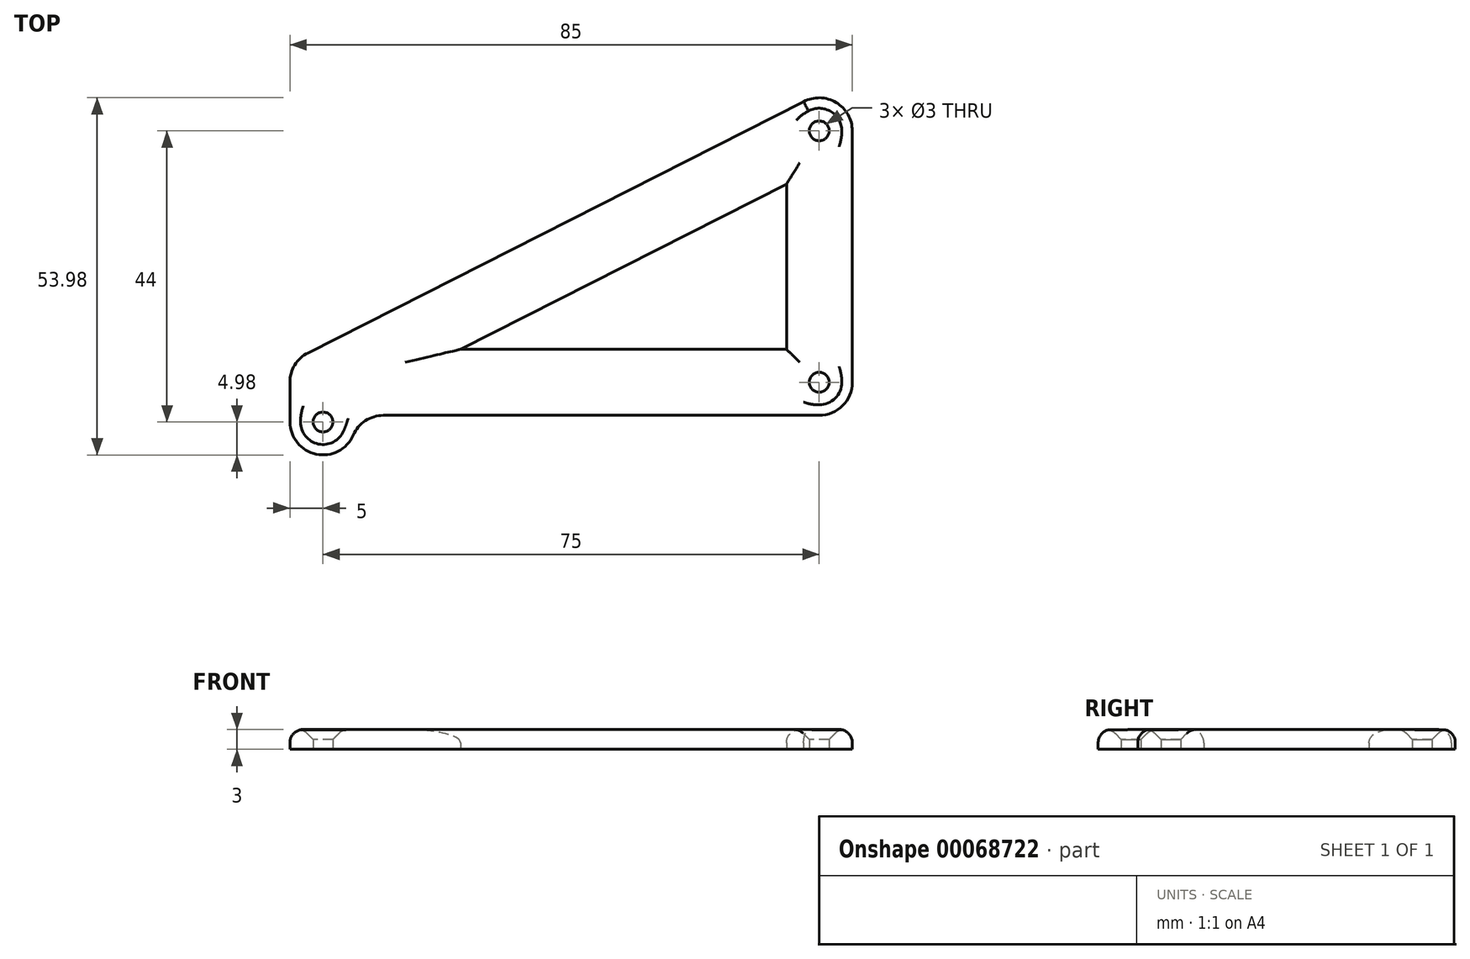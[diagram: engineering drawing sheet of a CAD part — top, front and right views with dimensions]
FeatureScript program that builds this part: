
annotation { "Feature Type Name" : "Feature", "Feature Type Description" : "" }
export const myFeature = defineFeature(function(context is Context, id is Id, definition is map)
    precondition{}
    {
        {
            var Q0;
            Q0=qCreatedBy(makeId("Top.planeOp"),FACE);
            var sketch = newSketch(context, id + "F0", { "sketchPlane" : qUnion([Q0])});
            skCircle(sketch, "E0", {"center": v(0, 0) * mm, "radius": 1.5 * mm});
            skCircle(sketch, "E1", {"center": v(0, 38) * mm, "radius": 1.5 * mm});
            skCircle(sketch, "E2", {"center": v(-75, -6) * mm, "radius": 1.5 * mm});
            skArc(sketch, "E3", {"start": v(-79.98, -6.02) * mm, "mid": v(-76.01, -10.87) * mm, "end": v(-70.44, -8) * mm});
            skArc(sketch, "E4", {"start": v(0, -5) * mm, "mid": v(3.54, -3.54) * mm, "end": v(5, 0) * mm});
            skArc(sketch, "E5", {"start": v(5, 38) * mm, "mid": v(2.57, 42.29) * mm, "end": v(-2.36, 42.41) * mm});
            skLineSegment(sketch, "E6", {"start": v(0, -5) * mm, "end": v(-65.86, -5) * mm});
            skLineSegment(sketch, "E7", {"start": v(-70.12, -5.04) * mm, "end": v(-70.12, -5) * mm});
            skLineSegment(sketch, "E8", {"start": v(-79.98, -6.02) * mm, "end": v(-80, 0) * mm});
            skLineSegment(sketch, "E9", {"start": v(-54.2, 5) * mm, "end": v(-4.95, 5) * mm});
            skLineSegment(sketch, "E10", {"start": v(5, 0) * mm, "end": v(5, 38) * mm});
            skLineSegment(sketch, "E11", {"start": v(-2.16, 42.5) * mm, "end": v(-77.27, 4.45) * mm});
            skLineSegment(sketch, "E12", {"start": v(-4.95, 29.95) * mm, "end": v(-4.95, 5) * mm});
            skPoint(sketch, "E13.trimOffspring.end.orphan", {"position": v(-4.95, 0) * mm});
            skPoint(sketch, "E14.trimOffspring.end.orphan", {"position": v(0, 5) * mm});
            skLineSegment(sketch, "E15.trimOffspring", {"start": v(-4.95, 29.95) * mm, "end": v(-54.2, 5) * mm});
            skPoint(sketch, "E16.center.orphan", {"position": v(-75, 0) * mm});
            skArc(sketch, "E17.trimOffspring", {"start": v(-77.25, 4.46) * mm, "mid": v(-79.26, 2.61) * mm, "end": v(-80, -0.02) * mm});
            skPoint(sketch, "E18.orphan", {"position": v(-70.12, 0) * mm});
            skPoint(sketch, "E19.visualSharp", {"position": v(-70.12, -5) * mm});
            skArc(sketch, "E19.filletArc", {"start": v(-65.86, -5) * mm, "mid": v(-68.6, -5.82) * mm, "end": v(-70.44, -8) * mm});
            skSolve(sketch);
        }
        {
            var Q0;
            Q0 = qSketchRegion(id + "F0", true);
            extrude(context, id + "F1", {"entities" : qUnion([Q0]), "depth" : 3 * mm});
        }
        {
            var Q0;
            Q0=makeQuery(id+"F1.opExtrude","CAP_EDGE",EDGE,{"disambiguationData":[OSD([sQuery(id+"F0.wireOp",EDGE,"E2")])],"isStart":false});
            var Q1;
            Q1=makeQuery(id+"F1.opExtrude","CAP_EDGE",EDGE,{"disambiguationData":[OSD([sQuery(id+"F0.wireOp",EDGE,"E0")])],"isStart":false});
            var Q2;
            Q2=makeQuery(id+"F1.opExtrude","CAP_EDGE",EDGE,{"disambiguationData":[OSD([sQuery(id+"F0.wireOp",EDGE,"E1")])],"isStart":false});
            chamfer(context, id + "F2", {"entities" : qUnion([Q0, Q1, Q2]), "width" : 1.5 * mm, "tangentPropagation" : true});
        }
        {
            var Q0;
            Q0=makeQuery(id+"F1.opExtrude","CAP_FACE",FACE,{"disambiguationData":[OSD([sQuery(id+"F0.wireOp",EDGE,"E0"),sQuery(id+"F0.wireOp",EDGE,"E1"),sQuery(id+"F0.wireOp",EDGE,"E2"),sQuery(id+"F0.wireOp",EDGE,"E3"),sQuery(id+"F0.wireOp",EDGE,"E4"),sQuery(id+"F0.wireOp",EDGE,"E5"),sQuery(id+"F0.wireOp",EDGE,"E6"),sQuery(id+"F0.wireOp",EDGE,"E8"),sQuery(id+"F0.wireOp",EDGE,"E9"),sQuery(id+"F0.wireOp",EDGE,"E10"),sQuery(id+"F0.wireOp",EDGE,"E11"),sQuery(id+"F0.wireOp",EDGE,"E12"),sQuery(id+"F0.wireOp",EDGE,"E15.trimOffspring"),sQuery(id+"F0.wireOp",EDGE,"E17.trimOffspring"),sQuery(id+"F0.wireOp",EDGE,"E19.filletArc")])],"isStart":false});
            fillet(context, id + "F3", {"entities" : qUnion([Q0]), "radius" : 2 * mm, "tangentPropagation" : true, "allowEdgeOverflow" : false});
        }
    });
